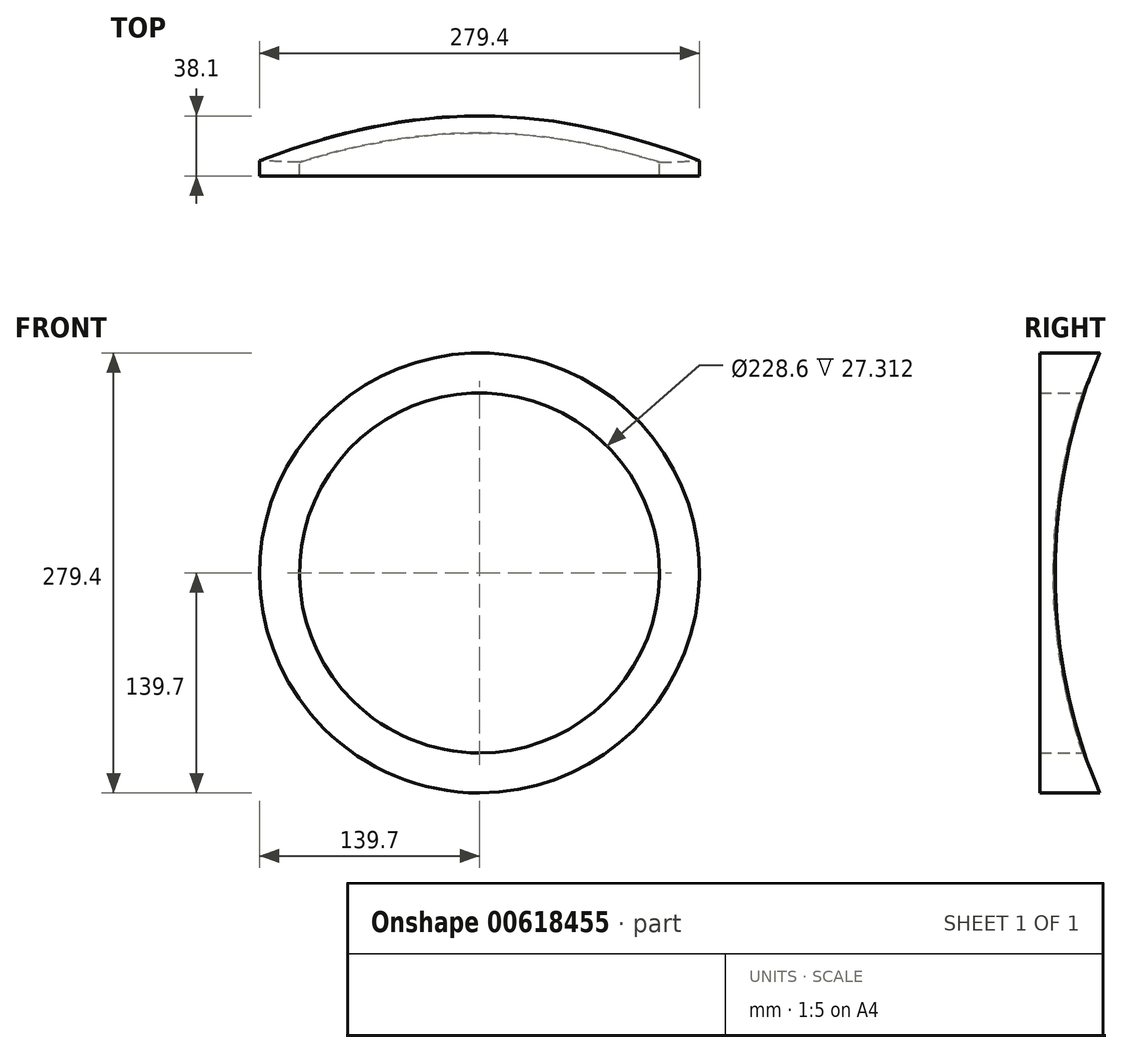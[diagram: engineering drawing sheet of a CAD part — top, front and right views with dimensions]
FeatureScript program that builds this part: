
annotation { "Feature Type Name" : "Feature", "Feature Type Description" : "" }
export const myFeature = defineFeature(function(context is Context, id is Id, definition is map)
    precondition{}
    {
        {
            var Q0;
            Q0=qCreatedBy(makeId("Front.planeOp"),FACE);
            var sketch = newSketch(context, id + "F0", { "sketchPlane" : qUnion([Q0])});
            skCircle(sketch, "E0", {"center": v(0, 0) * mm, "radius": 139.7 * mm});
            skCircle(sketch, "E1", {"center": v(0, 0) * mm, "radius": 114.3 * mm});
            skLineSegment(sketch, "E2", {"start": v(0, 139.7) * mm, "end": v(0, -139.7) * mm, "construction": true});
            skLineSegment(sketch, "E3", {"start": v(-139.7, 0) * mm, "end": v(139.7, 0) * mm, "construction": true});
            skSolve(sketch);
        }
        {
            var Q0;
            Q0 = qSketchRegion(id + "F0", true);
            extrude(context, id + "F1", {"entities" : qUnion([Q0]), "depth" : 38.1 * mm, "offsetDistance" : 25.4 * mm});
        }
        {
            var Q0;
            Q0=qCreatedBy(makeId("Right.planeOp"),FACE);
            var sketch = newSketch(context, id + "F2", { "sketchPlane" : qUnion([Q0])});
            skLineSegment(sketch, "E4.bottom", {"start": v(0, -139.7) * mm, "end": v(293.58, -139.7) * mm, "construction": true});
            skLineSegment(sketch, "E4.top", {"start": v(0, 139.7) * mm, "end": v(293.58, 139.7) * mm, "construction": true});
            skLineSegment(sketch, "E4.left", {"start": v(0, -139.7) * mm, "end": v(0, 139.7) * mm});
            skLineSegment(sketch, "E4.right", {"start": v(293.58, -139.7) * mm, "end": v(293.58, 139.7) * mm, "construction": true});
            skPoint(sketch, "E5", {"position": v(293.58, 0) * mm});
            skArc(sketch, "E6", {"start": v(0, 139.7) * mm, "mid": v(-31.54, 0) * mm, "end": v(0, -139.7) * mm});
            skLineSegment(sketch, "E7", {"start": v(0, 0) * mm, "end": v(293.58, 0) * mm, "construction": true});
            skSolve(sketch);
        }
        {
            var Q0;
            Q0=qCreatedBy(makeId("Top.planeOp"),FACE);
            var sketch = newSketch(context, id + "F3", { "sketchPlane" : qUnion([Q0])});
            skLineSegment(sketch, "E8.bottom", {"start": v(-139.7, 0) * mm, "end": v(139.7, 0) * mm});
            skLineSegment(sketch, "E8.top", {"start": v(-139.7, -3.18) * mm, "end": v(139.7, -3.18) * mm, "construction": true});
            skLineSegment(sketch, "E8.left", {"start": v(-139.7, 0) * mm, "end": v(-139.7, -3.17) * mm, "construction": true});
            skLineSegment(sketch, "E8.right", {"start": v(139.7, 0) * mm, "end": v(139.7, -3.17) * mm, "construction": true});
            skPoint(sketch, "E9", {"position": v(0, 0) * mm});
            skArc(sketch, "E10", {"start": v(-139.7, 0) * mm, "mid": v(0, -3.18) * mm, "end": v(139.7, 0) * mm});
            skSolve(sketch);
        }
        {
            var Q0;
            Q0 = qSketchRegion(id + "F2", true);
            var Q1;
            Q1=sQuery(id+"F3.wireOp",EDGE,"E10");
            sweep(context, id + "F4", {"operationType" : NewBodyOperationType.REMOVE, "profiles" : qUnion([Q0]), "path" : qUnion([Q1])});
        }
    });
